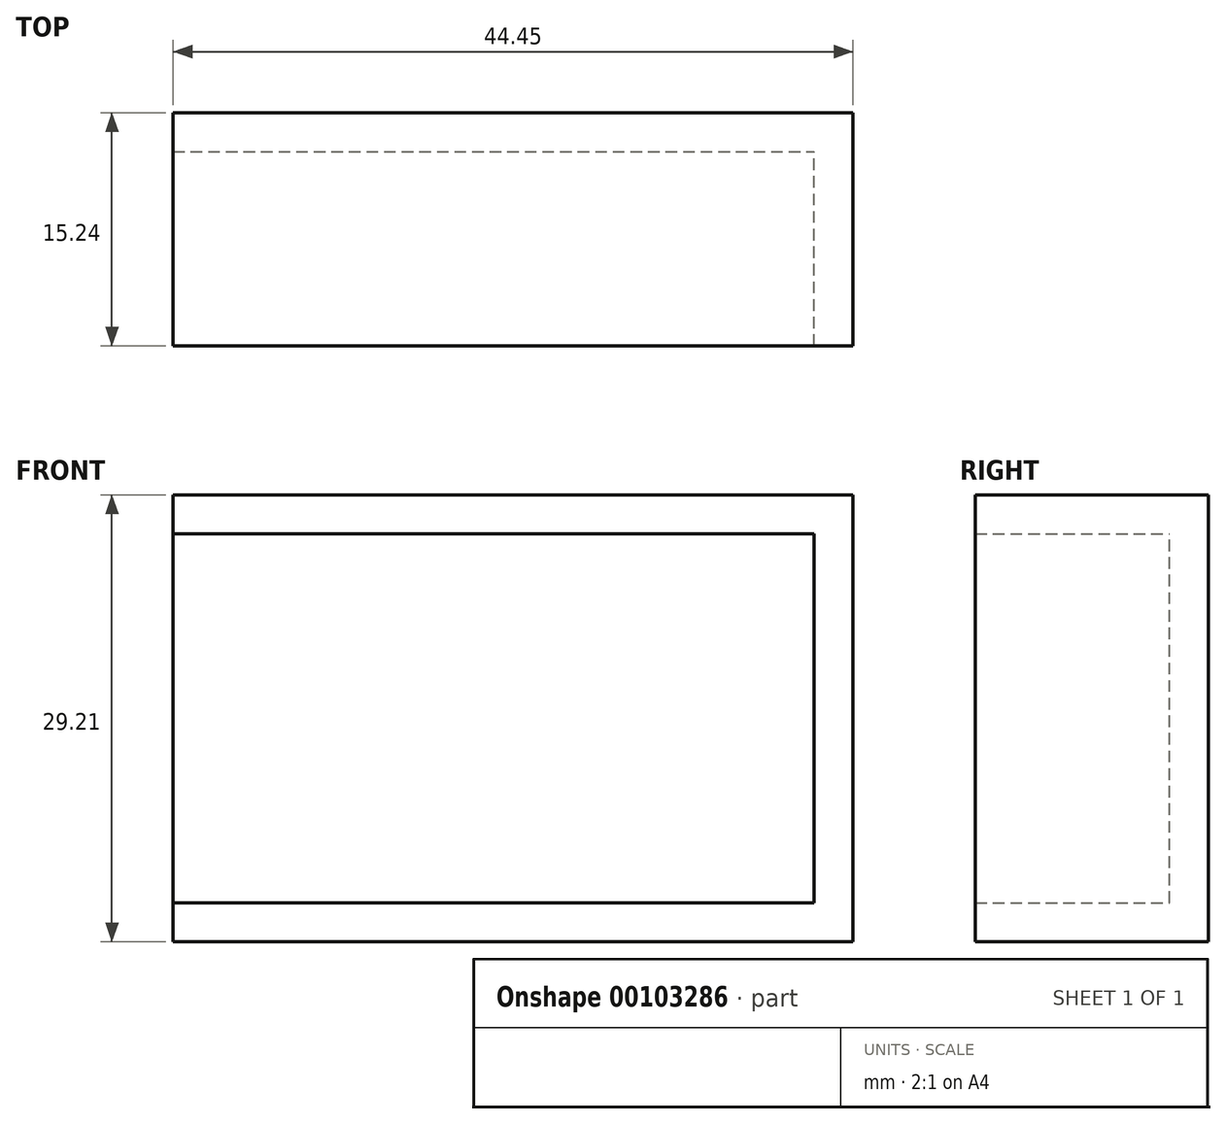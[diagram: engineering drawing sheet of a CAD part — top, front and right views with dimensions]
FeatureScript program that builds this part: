
annotation { "Feature Type Name" : "Feature", "Feature Type Description" : "" }
export const myFeature = defineFeature(function(context is Context, id is Id, definition is map)
    precondition{}
    {
        {
            var Q0;
            Q0=qCreatedBy(makeId("Front.planeOp"),FACE);
            var sketch = newSketch(context, id + "F0", { "sketchPlane" : qUnion([Q0])});
            skLineSegment(sketch, "E0.bottom", {"start": v(0, 0) * mm, "end": v(41.9, 0) * mm});
            skLineSegment(sketch, "E0.top", {"start": v(0, 24.13) * mm, "end": v(41.9, 24.13) * mm});
            skLineSegment(sketch, "E0.left", {"start": v(0, 0) * mm, "end": v(0, 24.13) * mm});
            skLineSegment(sketch, "E0.right", {"start": v(41.9, 0) * mm, "end": v(41.9, 24.13) * mm});
            skLineSegment(sketch, "E1.top", {"start": v(0, 26.67) * mm, "end": v(41.9, 26.67) * mm});
            skLineSegment(sketch, "E1.left", {"start": v(0, 24.13) * mm, "end": v(0, 26.67) * mm});
            skLineSegment(sketch, "E1.right", {"start": v(41.9, 24.13) * mm, "end": v(41.9, 26.67) * mm});
            skLineSegment(sketch, "E2.bottom", {"start": v(0, 0) * mm, "end": v(41.91, 0) * mm});
            skLineSegment(sketch, "E2.top", {"start": v(0, -2.54) * mm, "end": v(41.91, -2.54) * mm});
            skLineSegment(sketch, "E2.left", {"start": v(0, 0) * mm, "end": v(0, -2.54) * mm});
            skLineSegment(sketch, "E2.right", {"start": v(41.91, 0) * mm, "end": v(41.91, -2.54) * mm});
            skLineSegment(sketch, "E3.bottom", {"start": v(41.91, -2.54) * mm, "end": v(44.45, -2.54) * mm});
            skLineSegment(sketch, "E3.top", {"start": v(41.91, 26.67) * mm, "end": v(44.45, 26.67) * mm});
            skLineSegment(sketch, "E3.left", {"start": v(41.9, -2.54) * mm, "end": v(41.9, 26.67) * mm});
            skLineSegment(sketch, "E3.right", {"start": v(44.45, -2.54) * mm, "end": v(44.45, 26.67) * mm});
            skSolve(sketch);
        }
        {
            var Q0;
            {var subQ0=sQuery(id+"F0.wireOp",EDGE,"E0.top");Q0=makeQuery(id+"F0.imprint","IMPRINT",FACE,{"disambiguationData":[TD([[makeQuery(id+"F0.imprint","IMPRINT",EDGE,{"derivedFrom":subQ0}),1.0]])]});}
            var Q1;
            {var subQ3=sQuery(id+"F0.wireOp",EDGE,"E3.bottom");Q1=makeQuery(id+"F0.imprint","IMPRINT",FACE,{"disambiguationData":[TD([[makeQuery(id+"F0.imprint","IMPRINT",EDGE,{"derivedFrom":subQ3}),1.0]])]});}
            var Q2;
            {var subQ0=sQuery(id+"F0.wireOp",EDGE,"E2.bottom");Q2=makeQuery(id+"F0.imprint","IMPRINT",FACE,{"disambiguationData":[TD([[makeQuery(id+"F0.imprint","IMPRINT",EDGE,{"derivedFrom":subQ0}),-1.0]])]});}
            extrude(context, id + "F1", {"entities" : qUnion([Q0, Q1, Q2]), "depth" : 15.24 * mm});
        }
        {
            var Q0;
            Q0=makeQuery(id+"F0.imprint","IMPRINT",FACE,{"disambiguationData":[TD([[makeQuery(id+"F0.imprint","IMPRINT",EDGE,{"derivedFrom":sQuery(id+"F0.wireOp",EDGE,"E0.left")}),-1.0]])]});
            extrude(context, id + "F2", {"entities" : qUnion([Q0]), "operationType" : NewBodyOperationType.ADD, "depth" : 2.54 * mm});
        }
    });
